# Revit family: Gira_208900
name_source: partatom
category: Elektroinstallationen
revit_build: Autodesk Revit 2017 (Build: 20160225_1515(x64)
units: mm (PartAtom-declared; Revit-internal decimal feet)

## family parameters
Basisbauteil = Fläche
Beim Laden mit Abzugskörper schneiden = Nein
Bemaßung runder Anschluss = Durchmesser verwenden
Beschriftungsausrichtung beibehalten = Nein
Gemeinsam genutzt = Nein
Raumberechnungspunkt = Nein
Teiletyp = Normal

## types (1)
- Gira_208900
    Andere Bussysteme = ohne
    Ausführung = USB
    Ausführung der Oberfläche = nicht zutreffend
    BIM = https://media.stage.bim.site X1 REG KNX.rfa
    Beschreibung = Gira S1  REG Merkmale: - Sicherer Fernzugriff per Gira Smart Home App, HomeServer iOS App und Gira Sicherheitssystem iOS- und Android-App. - Sicherer Fernzugriff auf webbasierte Visualisierungen. - Sichere Fernwartung und Fernprogrammierung vom Gira HomeServer, Gira G1, Gira X1, Gira L1, Gira TKS-IP-Datenschnittstelle, Gira Sicherheitssystem Alarm Connect und Gira KNX IP-Router. - Sichere Fernprogrammierung über den Gira HomeServer-Experten. - Sichere Fernprogrammierung über den Gira Projekt Assistent (GPA). - Sichere Fernwartung und Fernprogrammierung von KNX Projekten mittels ETS4 oder ETS5. Unterstützt wird die Programmierung und Diagnose über Gruppen- und Busmonitor. - Sicherer Fernzugriff auf HTML-Seiten im Smart-Home-Netzwerk (z.B. Kamera, NAS, Router, Switch). - Sichere Datenübertragung mittels SSL TLS-Verschlüsselung. - Portalserver steht in Deutschland und unterliegt dem deutschen Datenrecht. - Unabhängigkeit vom Internetprovider und eingesetzten Routern. Sicherer Fernzugriff auch bei IPv6 Dual Stack Lite- (z.B. bei Unitymedia), LTE- oder UMTS-Anschlüssen. - Zugriffsmanagement der gesicherten Verbindungen über KNX Kommunikationsobjekte, Gira X1-App, Gira HomeServer-App und QuadClient. - Statussignalisierung der gesicherten Verbindungen über KNX Kommunikationsobjekte, Gira X1 App, Gira HomeServer App und QuadClient. - Benachrichtigungen per E-Mail versenden. Der E-Mail kann optional einen Anhang hinzugefügt werden. - Benachrichtigungen per SMS oder Sprachanruf versenden über den kostenpflichtigen Zusatzdienst sms77 oder MessageBird. - Auslöser der Benachrichtigungen können individuell konfiguriert werden (Filter, Bedingungen, Hysterese). - Bis zu 50 Benachrichtigungen werden unterstützt. - Optimierte KNX IP-Kommunikation, für mobile und sehr langsame Verbindungen. - Unterstützt die beschleunigte Übertragung von der ETS zu KNXnet IP Geräten über eine direkte KNX IP-Verbindung. - Zwei Buchsen RJ45 mit Switch-Funktionalität unterstützen das einfache Durchschleifen des Patchkabels. - Schnelle und komfortable Inbetriebnahme des Gira S1 über das Gira Geräteportal. - 2 GB Datenvolumen pro Monat. - Unbegrenzte Nutzungsdauer und 5 Jahre garantierter Serverbetrieb. - Funktionale Erweiterungen bzw. Aktualisierungen über Firmware- und Software-Updates. - Firmware-Update erfolgt über den Gira Projekt Assistent (GPA). - Hardware für KNX Secure vorbereitet. Zukünftiges Firmware-Update erforderlich.  Hinweise : - Versorgung über externe DC 24 V. - microSD-Karte nicht im Lieferumfang enthalten.
    Breite in Teilungseinheiten = 2
    Bussystem Funkbus = Nein
    Bussystem KNX = Ja
    Bussystem KNX-Funk = Nein
    Bussystem LON = Nein
    Bussystem Powernet = Nein
    DCF77 Empfänger integriert = Nein
    Datenblatt = https://katalog.gira.de
    Farbe = sonstige
    Funk bidirektional = Nein
    GTIN = 4010337035374
    HAN = 208900
    Hersteller = Gira
    IR-Sensor = Nein
    Logischer Baustein = Ja
    Mit Beschriftungsfeld = Nein
    Mit Busankopplung = Ja
    Mit Diebstahl-/Demontageschutz = Ja
    Mit Display = Ja
    Mit LED-Anzeige = Nein
    Montageart = REG
    Oberfläche = sonstige
    Produktseite = http://katalog.gira.de
    Präsenztaster = Nein
    Schutzart (IP) = IP20
    Status-LED = Ja
    Temperaturregler = Ja
    Transparent = Nein
    Typname = Abdeckrahmen 1f ClassiX Messing
    URL = https://www.gira.de
    Vorgabe-Ansicht = 1219 mm
    Werkstoff = sonstige
    Werkstoffgüte = sonstige
    Zentrale Funktionseinheit für Sender/Aktoren = Ja

## geometry (parser evidence)
native form markers: Sweep x2
no freeform markers — native parametric forms only
